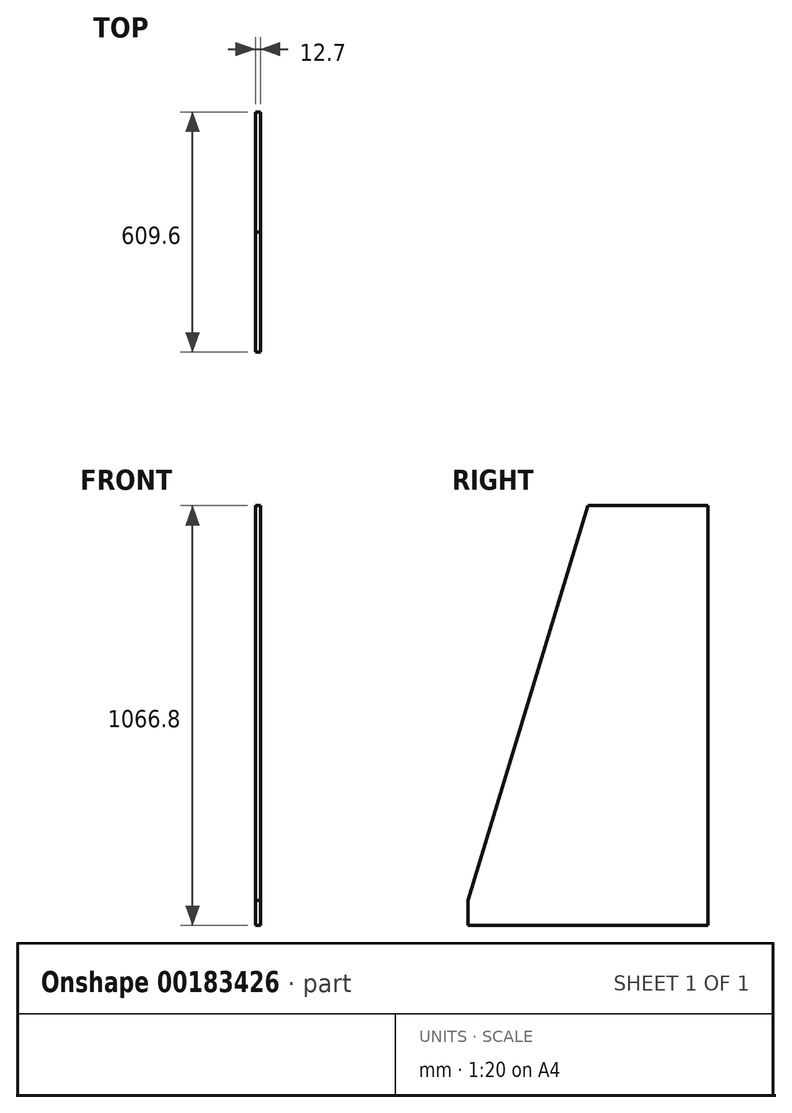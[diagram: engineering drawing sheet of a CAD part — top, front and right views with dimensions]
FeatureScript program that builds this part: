
annotation { "Feature Type Name" : "Feature", "Feature Type Description" : "" }
export const myFeature = defineFeature(function(context is Context, id is Id, definition is map)
    precondition{}
    {
        {
            var Q0;
            Q0=qCreatedBy(makeId("Right.planeOp"),FACE);
            var sketch = newSketch(context, id + "F0", { "sketchPlane" : qUnion([Q0])});
            skLineSegment(sketch, "E0.bottom", {"start": v(0, 0) * mm, "end": v(-609.6, 0) * mm});
            skLineSegment(sketch, "E0.top", {"start": v(0, 1066.8) * mm, "end": v(-304.8, 1066.8) * mm});
            skLineSegment(sketch, "E0.left", {"start": v(0, 0) * mm, "end": v(0, 1066.8) * mm});
            skLineSegment(sketch, "E0.right", {"start": v(-609.6, 0) * mm, "end": v(-609.6, 63.5) * mm});
            skLineSegment(sketch, "E1", {"start": v(-304.8, 1066.8) * mm, "end": v(-609.6, 63.5) * mm});
            skSolve(sketch);
        }
        {
            var Q0;
            Q0=makeQuery(id+"F0.imprint","IMPRINT",FACE,{"disambiguationData":[TD([[makeQuery(id+"F0.imprint","IMPRINT",EDGE,{"derivedFrom":sQuery(id+"F0.wireOp",EDGE,"E0.bottom")}),-1.0]])]});
            extrude(context, id + "F1", {"entities" : qUnion([Q0]), "depth" : 12.7 * mm});
        }
    });
